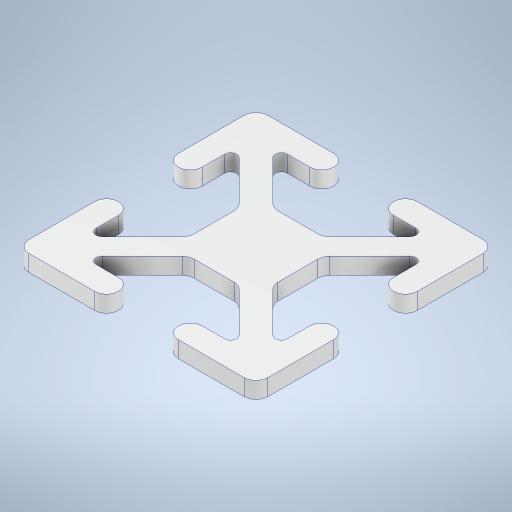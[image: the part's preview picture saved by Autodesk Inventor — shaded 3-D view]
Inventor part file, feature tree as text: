
AUTODESK INVENTOR PART (.ipt)
format: ipt  version: 2024 (Build 280153000, 153)  size: 353,280 bytes
history: native  units: in
note: dims shown in document units (in); Inventor stores cm internally (conversion verified against a paired STEP export)
features: fillet x2, extrude x1, sketch x1
ambient origin geometry x8: Origin, YZ Plane, XZ Plane, XY Plane, X Axis, Y Axis, Z Axis, Center Point
bodies: Solid1 (feature_tree)
feature tree (4):
  extrude  "Extrusion1"  Depth=1.0in
  fillet  "Fillet1"  Radius=0.8in
  fillet  "Fillet2"  Radius=0.8in
  sketch  "Sketch1"  dims[d0=1.0in d1=1.0in d2=0.8in d3=0.8in d4=0.35in d5=0.35in d6=0.125in d7=0.25in d8=0.125in d9=0.25in d10=0.1in d11=0.1in d12=0.069in d13=0.0in d14=0.05in d15=0.025in]
